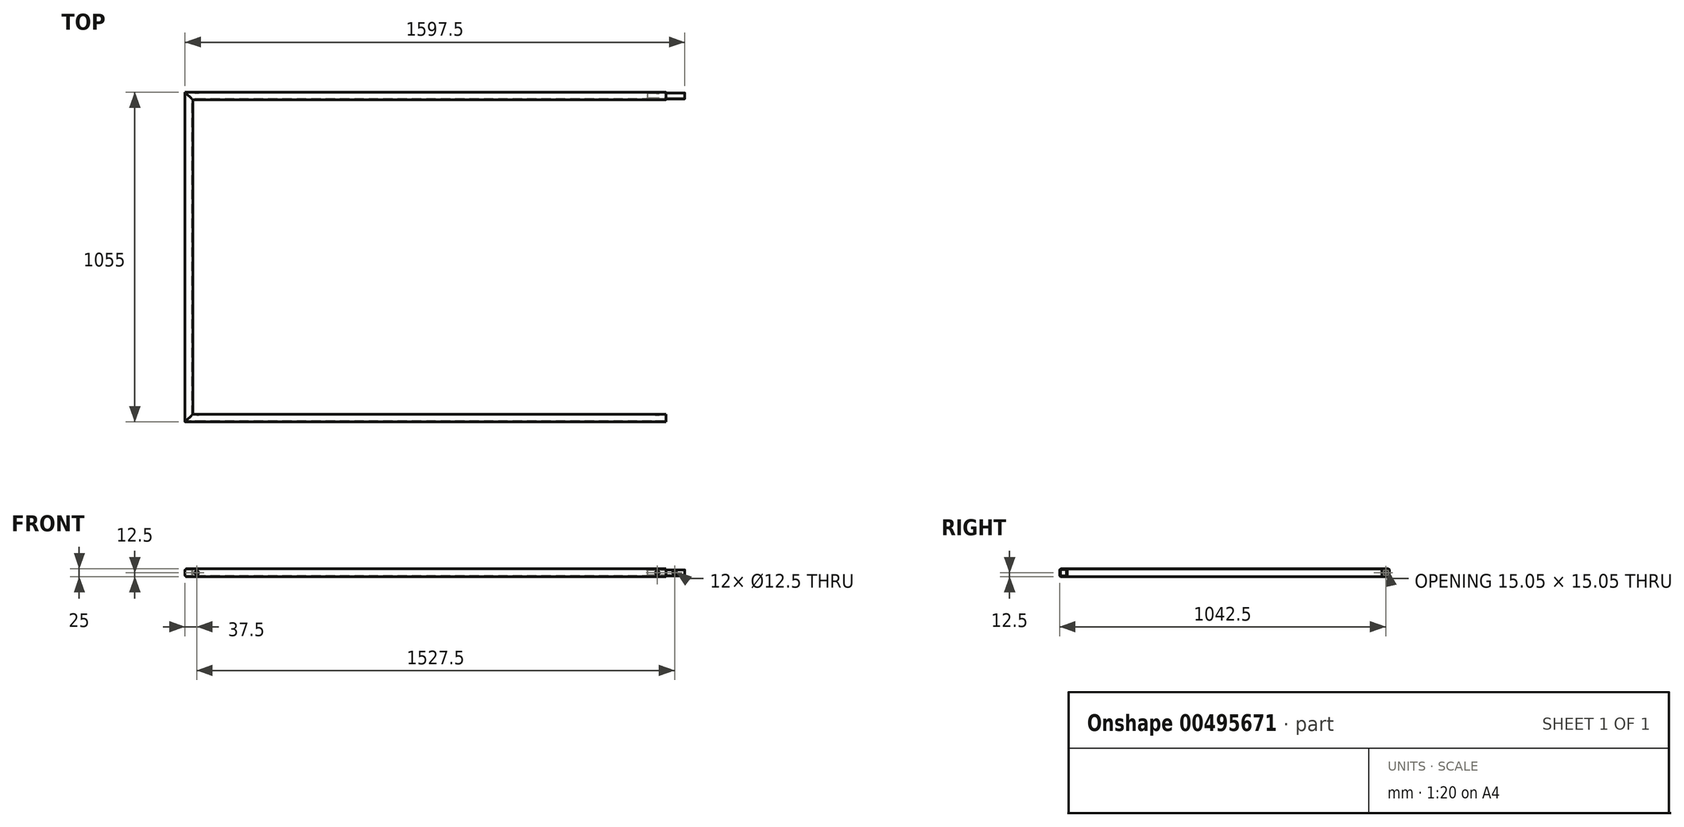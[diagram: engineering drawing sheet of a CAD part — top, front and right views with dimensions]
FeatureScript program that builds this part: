
annotation { "Feature Type Name" : "Feature", "Feature Type Description" : "" }
export const myFeature = defineFeature(function(context is Context, id is Id, definition is map)
    precondition{}
    {
        {
            var Q0;
            Q0=qCreatedBy(makeId("Right.planeOp"),FACE);
            var sketch = newSketch(context, id + "F0", { "sketchPlane" : qUnion([Q0])});
            skLineSegment(sketch, "E0.bottom", {"start": v(522.5, 12.5) * mm, "end": v(507.5, 12.5) * mm});
            skLineSegment(sketch, "E0.top", {"start": v(522.5, -12.5) * mm, "end": v(507.5, -12.5) * mm});
            skLineSegment(sketch, "E0.left", {"start": v(527.5, 7.5) * mm, "end": v(527.5, -7.5) * mm});
            skLineSegment(sketch, "E0.right", {"start": v(502.5, 7.5) * mm, "end": v(502.5, -7.5) * mm});
            skPoint(sketch, "E0.middle", {"position": v(515, 0) * mm});
            skPoint(sketch, "E1.visualSharp", {"position": v(502.5, 12.5) * mm});
            skArc(sketch, "E1.filletArc", {"start": v(507.5, 12.5) * mm, "mid": v(503.96, 11.04) * mm, "end": v(502.5, 7.5) * mm});
            skPoint(sketch, "E2.visualSharp", {"position": v(527.5, 12.5) * mm});
            skArc(sketch, "E2.filletArc", {"start": v(527.5, 7.5) * mm, "mid": v(526.04, 11.04) * mm, "end": v(522.5, 12.5) * mm});
            skPoint(sketch, "E3.visualSharp", {"position": v(527.5, -12.5) * mm});
            skArc(sketch, "E3.filletArc", {"start": v(522.5, -12.5) * mm, "mid": v(526.04, -11.04) * mm, "end": v(527.5, -7.5) * mm});
            skPoint(sketch, "E4.visualSharp", {"position": v(502.5, -12.5) * mm});
            skArc(sketch, "E4.filletArc", {"start": v(502.5, -7.5) * mm, "mid": v(503.96, -11.04) * mm, "end": v(507.5, -12.5) * mm});
            skArc(sketch, "E5.0", {"start": v(525, 7.5) * mm, "mid": v(524.27, 9.27) * mm, "end": v(522.5, 10) * mm});
            skLineSegment(sketch, "E5.1", {"start": v(525, 7.5) * mm, "end": v(525, -7.5) * mm});
            skLineSegment(sketch, "E5.2", {"start": v(522.5, 10) * mm, "end": v(507.5, 10) * mm});
            skArc(sketch, "E5.3", {"start": v(522.5, -10) * mm, "mid": v(524.27, -9.27) * mm, "end": v(525, -7.5) * mm});
            skArc(sketch, "E5.4", {"start": v(507.5, 10) * mm, "mid": v(505.73, 9.27) * mm, "end": v(505, 7.5) * mm});
            skLineSegment(sketch, "E5.5", {"start": v(505, 7.5) * mm, "end": v(505, -7.5) * mm});
            skArc(sketch, "E5.6", {"start": v(505, -7.5) * mm, "mid": v(505.73, -9.27) * mm, "end": v(507.5, -10) * mm});
            skLineSegment(sketch, "E5.7", {"start": v(522.5, -10) * mm, "end": v(507.5, -10) * mm});
            skSolve(sketch);
        }
        {
            var Q0;
            Q0 = qSketchRegion(id + "F0", true);
            extrude(context, id + "F1", {"entities" : qUnion([Q0]), "depth" : 1537.5 * mm});
        }
        {
            var Q0;
            Q0=makeQuery(id+"F1.opExtrude","SWEPT_FACE",FACE,{"disambiguationData":[OSD([sQuery(id+"F0.wireOp",EDGE,"E0.bottom")])]});
            var sketch = newSketch(context, id + "F2", { "sketchPlane" : qUnion([Q0])});
            skLineSegment(sketch, "E6", {"start": v(0, 527.5) * mm, "end": v(25, 502.5) * mm});
            skLineSegment(sketch, "E7", {"start": v(25, 502.5) * mm, "end": v(0, 502.5) * mm});
            skLineSegment(sketch, "E8", {"start": v(0, 502.5) * mm, "end": v(0, 527.5) * mm});
            skSolve(sketch);
        }
        {
            var Q0;
            Q0 = qSketchRegion(id + "F2", true);
            extrude(context, id + "F3", {"entities" : qUnion([Q0]), "operationType" : NewBodyOperationType.REMOVE, "endBound" : BoundingType.THROUGH_ALL, "oppositeDirection" : true, "depth" : 25 * mm});
        }
        {
            var Q0;
            Q0=qCreatedBy(makeId("Front.planeOp"),FACE);
            var sketch = newSketch(context, id + "F4", { "sketchPlane" : qUnion([Q0])});
            skLineSegment(sketch, "E9.0", {"start": v(5, 12.5) * mm, "end": v(20, 12.5) * mm});
            skArc(sketch, "E9.1", {"start": v(5, 12.5) * mm, "mid": v(1.46, 11.04) * mm, "end": v(0, 7.5) * mm});
            skLineSegment(sketch, "E9.2", {"start": v(0, 7.5) * mm, "end": v(0, -7.5) * mm});
            skArc(sketch, "E9.3", {"start": v(0, -7.5) * mm, "mid": v(1.46, -11.04) * mm, "end": v(5, -12.5) * mm});
            skLineSegment(sketch, "E9.4", {"start": v(20, -12.5) * mm, "end": v(5, -12.5) * mm});
            skArc(sketch, "E9.5", {"start": v(20, -12.5) * mm, "mid": v(23.54, -11.04) * mm, "end": v(25, -7.5) * mm});
            skLineSegment(sketch, "E9.6", {"start": v(25, -7.5) * mm, "end": v(25, 7.5) * mm});
            skArc(sketch, "E9.7", {"start": v(25, 7.5) * mm, "mid": v(23.54, 11.04) * mm, "end": v(20, 12.5) * mm});
            skArc(sketch, "E9.8", {"start": v(5, 10) * mm, "mid": v(3.23, 9.27) * mm, "end": v(2.5, 7.5) * mm});
            skLineSegment(sketch, "E9.9", {"start": v(20, 10) * mm, "end": v(5, 10) * mm});
            skArc(sketch, "E9.10", {"start": v(22.5, 7.5) * mm, "mid": v(21.77, 9.27) * mm, "end": v(20, 10) * mm});
            skLineSegment(sketch, "E9.11", {"start": v(22.5, -7.5) * mm, "end": v(22.5, 7.5) * mm});
            skLineSegment(sketch, "E9.12", {"start": v(2.5, -7.5) * mm, "end": v(2.5, 7.5) * mm});
            skArc(sketch, "E9.13", {"start": v(2.5, -7.5) * mm, "mid": v(3.23, -9.27) * mm, "end": v(5, -10) * mm});
            skLineSegment(sketch, "E9.14", {"start": v(20, -10) * mm, "end": v(5, -10) * mm});
            skArc(sketch, "E9.15", {"start": v(20, -10) * mm, "mid": v(21.77, -9.27) * mm, "end": v(22.5, -7.5) * mm});
            skSolve(sketch);
        }
        {
            var Q0;
            Q0 = qSketchRegion(id + "F4", true);
            extrude(context, id + "F5", {"entities" : qUnion([Q0]), "endBound" : BoundingType.UP_TO_NEXT, "oppositeDirection" : true, "depth" : 25 * mm});
        }
        {
            var Q0;
            Q0=makeQuery(id+"F5.opExtrude","SWEPT_BODY",BODY,{"disambiguationData":[OSD([sQuery(id+"F4.wireOp",EDGE,"E9.0"),sQuery(id+"F4.wireOp",EDGE,"E9.1"),sQuery(id+"F4.wireOp",EDGE,"E9.2"),sQuery(id+"F4.wireOp",EDGE,"E9.3"),sQuery(id+"F4.wireOp",EDGE,"E9.4"),sQuery(id+"F4.wireOp",EDGE,"E9.5"),sQuery(id+"F4.wireOp",EDGE,"E9.6"),sQuery(id+"F4.wireOp",EDGE,"E9.7"),sQuery(id+"F4.wireOp",EDGE,"E9.8"),sQuery(id+"F4.wireOp",EDGE,"E9.9"),sQuery(id+"F4.wireOp",EDGE,"E9.10"),sQuery(id+"F4.wireOp",EDGE,"E9.11"),sQuery(id+"F4.wireOp",EDGE,"E9.12"),sQuery(id+"F4.wireOp",EDGE,"E9.13"),sQuery(id+"F4.wireOp",EDGE,"E9.14"),sQuery(id+"F4.wireOp",EDGE,"E9.15")])]});
            var Q1;
            Q1=qCreatedBy(makeId("Front.planeOp"),FACE);
            mirror(context, id + "F6", {"operationType" : NewBodyOperationType.ADD, "entities" : qUnion([Q0]), "mirrorPlane" : qUnion([Q1])});
        }
        {
            var Q0;
            Q0=makeQuery(id+"F1.opExtrude","SWEPT_FACE",FACE,{"disambiguationData":[OSD([sQuery(id+"F0.wireOp",EDGE,"E0.left")])]});
            var sketch = newSketch(context, id + "F7", { "sketchPlane" : qUnion([Q0])});
            skLineSegment(sketch, "E10", {"start": v(-1537.5, 0) * mm, "end": v(-1510, 0) * mm, "construction": true});
            skCircle(sketch, "E11", {"center": v(-1510, 0) * mm, "radius": 6.25 * mm});
            skSolve(sketch);
        }
        {
            var Q0;
            Q0=makeQuery(id+"F1.opExtrude","SWEPT_FACE",FACE,{"disambiguationData":[OSD([sQuery(id+"F0.wireOp",EDGE,"E0.right")])]});
            var sketch = newSketch(context, id + "F8", { "sketchPlane" : qUnion([Q0])});
            skLineSegment(sketch, "E12", {"start": v(25, 0) * mm, "end": v(37.5, 0) * mm, "construction": true});
            skCircle(sketch, "E13", {"center": v(37.5, 0) * mm, "radius": 6.25 * mm});
            skSolve(sketch);
        }
        {
            var Q0;
            Q0 = qSketchRegion(id + "F8", true);
            extrude(context, id + "F9", {"entities" : qUnion([Q0]), "operationType" : NewBodyOperationType.REMOVE, "endBound" : BoundingType.THROUGH_ALL, "oppositeDirection" : true, "depth" : 25 * mm});
        }
        {
            var Q0;
            Q0 = qSketchRegion(id + "F7", true);
            extrude(context, id + "F10", {"entities" : qUnion([Q0]), "operationType" : NewBodyOperationType.REMOVE, "endBound" : BoundingType.THROUGH_ALL, "oppositeDirection" : true, "depth" : 25 * mm});
        }
        {
            var Q0;
            Q0=makeQuery(id+"F1.opExtrude","SWEPT_BODY",BODY,{"disambiguationData":[OSD([sQuery(id+"F0.wireOp",EDGE,"E0.bottom"),sQuery(id+"F0.wireOp",EDGE,"E0.top"),sQuery(id+"F0.wireOp",EDGE,"E0.left"),sQuery(id+"F0.wireOp",EDGE,"E0.right"),sQuery(id+"F0.wireOp",EDGE,"E1.filletArc"),sQuery(id+"F0.wireOp",EDGE,"E2.filletArc"),sQuery(id+"F0.wireOp",EDGE,"E3.filletArc"),sQuery(id+"F0.wireOp",EDGE,"E4.filletArc"),sQuery(id+"F0.wireOp",EDGE,"E5.0"),sQuery(id+"F0.wireOp",EDGE,"E5.1"),sQuery(id+"F0.wireOp",EDGE,"E5.2"),sQuery(id+"F0.wireOp",EDGE,"E5.3"),sQuery(id+"F0.wireOp",EDGE,"E5.4"),sQuery(id+"F0.wireOp",EDGE,"E5.5"),sQuery(id+"F0.wireOp",EDGE,"E5.6"),sQuery(id+"F0.wireOp",EDGE,"E5.7")])]});
            var Q1;
            Q1=qCreatedBy(makeId("Front.planeOp"),FACE);
            mirror(context, id + "F11", {"entities" : qUnion([Q0]), "mirrorPlane" : qUnion([Q1])});
        }
        {
            var Q0;
            Q0=makeQuery(id+"F1.opExtrude","CAP_FACE",FACE,{"disambiguationData":[OSD([sQuery(id+"F0.wireOp",EDGE,"E0.bottom"),sQuery(id+"F0.wireOp",EDGE,"E0.top"),sQuery(id+"F0.wireOp",EDGE,"E0.left"),sQuery(id+"F0.wireOp",EDGE,"E0.right"),sQuery(id+"F0.wireOp",EDGE,"E1.filletArc"),sQuery(id+"F0.wireOp",EDGE,"E2.filletArc"),sQuery(id+"F0.wireOp",EDGE,"E3.filletArc"),sQuery(id+"F0.wireOp",EDGE,"E4.filletArc"),sQuery(id+"F0.wireOp",EDGE,"E5.0"),sQuery(id+"F0.wireOp",EDGE,"E5.1"),sQuery(id+"F0.wireOp",EDGE,"E5.2"),sQuery(id+"F0.wireOp",EDGE,"E5.3"),sQuery(id+"F0.wireOp",EDGE,"E5.4"),sQuery(id+"F0.wireOp",EDGE,"E5.5"),sQuery(id+"F0.wireOp",EDGE,"E5.6"),sQuery(id+"F0.wireOp",EDGE,"E5.7")])],"isStart":false});
            var sketch = newSketch(context, id + "F12", { "sketchPlane" : qUnion([Q0])});
            skLineSegment(sketch, "E14.bottom", {"start": v(520.53, 9.53) * mm, "end": v(509.48, 9.53) * mm});
            skLineSegment(sketch, "E14.top", {"start": v(520.53, -9.52) * mm, "end": v(509.48, -9.52) * mm});
            skLineSegment(sketch, "E14.left", {"start": v(524.53, 5.53) * mm, "end": v(524.53, -5.52) * mm});
            skLineSegment(sketch, "E14.right", {"start": v(505.48, 5.53) * mm, "end": v(505.48, -5.52) * mm});
            skPoint(sketch, "E14.middle", {"position": v(515, 0) * mm});
            skPoint(sketch, "E14.middle.positionSnap0", {"position": v(515, 12.5) * mm});
            skPoint(sketch, "E14.middle.positionSnap1", {"position": v(527.5, 0) * mm});
            skPoint(sketch, "E14.centerSnap0", {"position": v(515, 12.5) * mm});
            skPoint(sketch, "E14.centerSnap1", {"position": v(527.5, 0) * mm});
            skPoint(sketch, "E15.visualSharp", {"position": v(505.48, 9.53) * mm});
            skArc(sketch, "E15.filletArc", {"start": v(509.48, 9.53) * mm, "mid": v(506.65, 8.35) * mm, "end": v(505.48, 5.53) * mm});
            skPoint(sketch, "E16.visualSharp", {"position": v(524.53, 9.53) * mm});
            skArc(sketch, "E16.filletArc", {"start": v(524.53, 5.53) * mm, "mid": v(523.35, 8.35) * mm, "end": v(520.53, 9.53) * mm});
            skPoint(sketch, "E17.visualSharp", {"position": v(524.53, -9.52) * mm});
            skArc(sketch, "E17.filletArc", {"start": v(520.53, -9.52) * mm, "mid": v(523.35, -8.35) * mm, "end": v(524.53, -5.52) * mm});
            skPoint(sketch, "E18.visualSharp", {"position": v(505.48, -9.52) * mm});
            skArc(sketch, "E18.filletArc", {"start": v(505.48, -5.52) * mm, "mid": v(506.65, -8.35) * mm, "end": v(509.48, -9.52) * mm});
            skLineSegment(sketch, "E19.0", {"start": v(522.53, 5.53) * mm, "end": v(522.53, -5.52) * mm});
            skArc(sketch, "E19.1", {"start": v(520.53, -7.52) * mm, "mid": v(521.94, -6.94) * mm, "end": v(522.53, -5.52) * mm});
            skArc(sketch, "E19.2", {"start": v(522.53, 5.53) * mm, "mid": v(521.94, 6.94) * mm, "end": v(520.53, 7.53) * mm});
            skLineSegment(sketch, "E19.3", {"start": v(520.53, -7.52) * mm, "end": v(509.48, -7.52) * mm});
            skLineSegment(sketch, "E19.4", {"start": v(520.53, 7.53) * mm, "end": v(509.48, 7.53) * mm});
            skArc(sketch, "E19.5", {"start": v(509.48, 7.53) * mm, "mid": v(508.06, 6.94) * mm, "end": v(507.48, 5.53) * mm});
            skLineSegment(sketch, "E19.6", {"start": v(507.48, 5.53) * mm, "end": v(507.48, -5.52) * mm});
            skArc(sketch, "E19.7", {"start": v(507.48, -5.52) * mm, "mid": v(508.06, -6.94) * mm, "end": v(509.48, -7.52) * mm});
            skSolve(sketch);
        }
        {
            var Q0;
            Q0 = qSketchRegion(id + "F12", true);
            extrude(context, id + "F13", {"entities" : qUnion([Q0]), "endBound" : BoundingType.SYMMETRIC, "depth" : 120 * mm});
        }
        {
            var Q0;
            Q0=makeQuery(id+"F13.opExtrude","SWEPT_FACE",FACE,{"disambiguationData":[OSD([sQuery(id+"F12.wireOp",EDGE,"E14.left")])]});
            var sketch = newSketch(context, id + "F14", { "sketchPlane" : qUnion([Q0])});
            skCircle(sketch, "E20", {"center": v(-1565, 0) * mm, "radius": 6.25 * mm});
            skLineSegment(sketch, "E21", {"start": v(-1537.5, 0) * mm, "end": v(-1537.5, 5.52) * mm, "construction": true});
            skPoint(sketch, "E21.startSnap0", {"position": v(-1537.5, 5.52) * mm});
            skCircle(sketch, "E22.MirrorC", {"center": v(-1510, 0) * mm, "radius": 6.25 * mm});
            skSolve(sketch);
        }
        {
            var Q0;
            Q0 = qSketchRegion(id + "F14", true);
            extrude(context, id + "F15", {"entities" : qUnion([Q0]), "operationType" : NewBodyOperationType.REMOVE, "oppositeDirection" : true, "depth" : 25 * mm});
        }
    });
